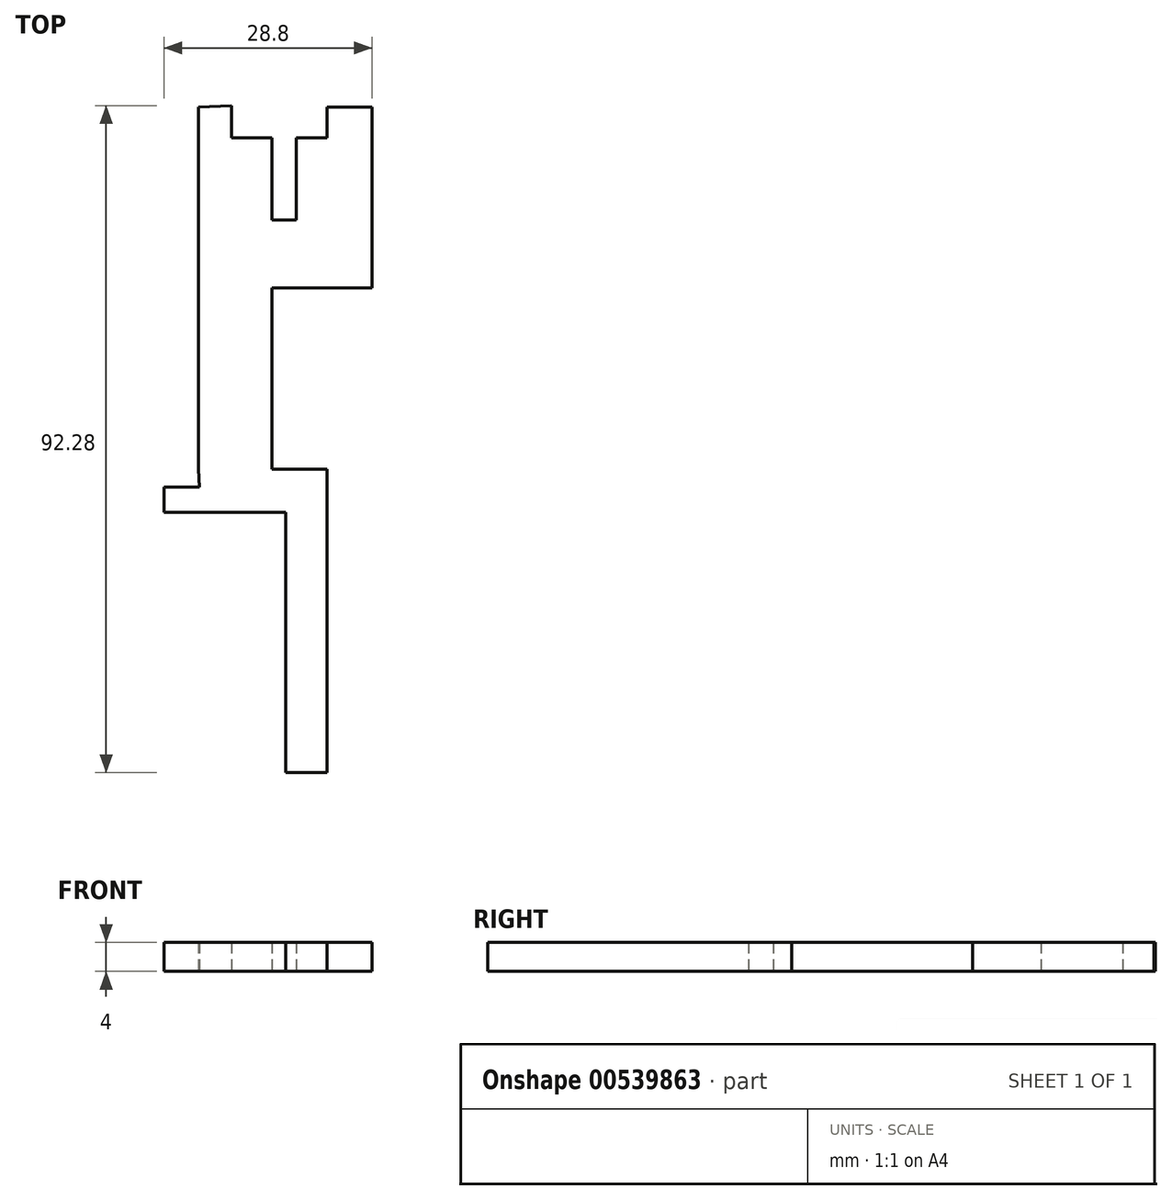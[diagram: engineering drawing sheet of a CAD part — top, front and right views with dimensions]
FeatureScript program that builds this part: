
annotation { "Feature Type Name" : "Feature", "Feature Type Description" : "" }
export const myFeature = defineFeature(function(context is Context, id is Id, definition is map)
    precondition{}
    {
        {
            var Q0;
            Q0=qCreatedBy(makeId("Top.planeOp"),FACE);
            var sketch = newSketch(context, id + "F0", { "sketchPlane" : qUnion([Q0])});
            skLineSegment(sketch, "E0.right", {"start": v(-13.39, 2.15) * mm, "end": v(-13.39, 5.96) * mm});
            skLineSegment(sketch, "E1.left", {"start": v(-21, 5.96) * mm, "end": v(-21, 31) * mm});
            skLineSegment(sketch, "E1.right", {"start": v(-31.16, 5.96) * mm, "end": v(-31.16, 56.05) * mm});
            skLineSegment(sketch, "E2", {"start": v(-21, 31) * mm, "end": v(-7.14, 31) * mm});
            skLineSegment(sketch, "E3", {"start": v(-7.14, 31) * mm, "end": v(-7.14, 56.05) * mm});
            skLineSegment(sketch, "E4", {"start": v(-7.14, 56.05) * mm, "end": v(-13.42, 56.05) * mm});
            skLineSegment(sketch, "E5", {"start": v(-13.42, 56.05) * mm, "end": v(-13.42, 51.77) * mm});
            skLineSegment(sketch, "E6", {"start": v(-13.42, 51.77) * mm, "end": v(-17.67, 51.77) * mm});
            skLineSegment(sketch, "E7", {"start": v(-17.67, 51.77) * mm, "end": v(-17.67, 40.42) * mm});
            skLineSegment(sketch, "E8", {"start": v(-17.67, 40.42) * mm, "end": v(-21, 40.42) * mm});
            skPoint(sketch, "E9.orphan", {"position": v(-21, 56.05) * mm});
            skLineSegment(sketch, "E10", {"start": v(-21, 40.42) * mm, "end": v(-21, 51.77) * mm});
            skLineSegment(sketch, "E11", {"start": v(-21, 51.77) * mm, "end": v(-26.6, 51.77) * mm});
            skLineSegment(sketch, "E12", {"start": v(-26.6, 51.77) * mm, "end": v(-26.6, 56.23) * mm});
            skLineSegment(sketch, "E13", {"start": v(-26.6, 56.23) * mm, "end": v(-31.16, 56.05) * mm});
            skLineSegment(sketch, "E14.trimOffspring", {"start": v(-21, 5.96) * mm, "end": v(-13.39, 5.96) * mm});
            skLineSegment(sketch, "E15", {"start": v(-13.39, 2.15) * mm, "end": v(-13.39, -36.05) * mm});
            skLineSegment(sketch, "E16", {"start": v(-13.39, -36.05) * mm, "end": v(-19.08, -36.05) * mm});
            skLineSegment(sketch, "E17", {"start": v(-19.08, -36.05) * mm, "end": v(-19.08, 0) * mm});
            skLineSegment(sketch, "E18", {"start": v(-19.08, 0) * mm, "end": v(-31.68, 0) * mm});
            skLineSegment(sketch, "E19", {"start": v(-31.68, 0) * mm, "end": v(-35.94, 0) * mm});
            skLineSegment(sketch, "E20", {"start": v(-35.94, 0) * mm, "end": v(-35.94, 3.45) * mm});
            skLineSegment(sketch, "E21", {"start": v(-35.94, 3.45) * mm, "end": v(-31.06, 3.45) * mm});
            skLineSegment(sketch, "E22", {"start": v(-31.06, 3.45) * mm, "end": v(-31.16, 5.96) * mm});
            skSolve(sketch);
        }
        {
            var Q0;
            Q0=makeQuery(id+"F0.imprint","IMPRINT",FACE,{"disambiguationData":[TD([[makeQuery(id+"F0.imprint","IMPRINT",EDGE,{"derivedFrom":sQuery(id+"F0.wireOp",EDGE,"E0.right")}),1.0]])]});
            extrude(context, id + "F1", {"entities" : qUnion([Q0]), "depth" : 4 * mm, "offsetDistance" : 25 * mm});
        }
    });
